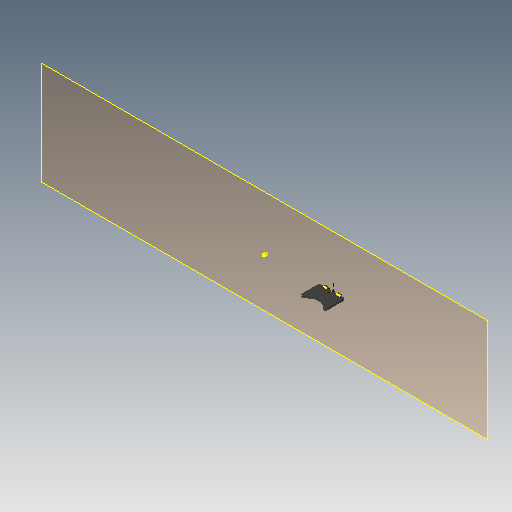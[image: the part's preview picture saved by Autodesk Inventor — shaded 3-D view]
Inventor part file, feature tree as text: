
AUTODESK INVENTOR PART (.ipt)
format: ipt  version: 2017 (Build 210142000, 142)  size: 185,856 bytes
history: native  units: mm
features: sketch x7, extrude x6, fillet x2, reference x2, projected_geometry x2, other x2, plane x1
ambient origin geometry x8: Origin, YZ Plane, XZ Plane, XY Plane, X Axis, Y Axis, Z Axis, Center Point
bodies: Solid1 (feature_tree)
feature tree (22):
  plane  "Work Plane1"
  extrude  "Extrusion1"  Depth=3.0mm
  sketch  "Sketch2"  dims[d2=6.0mm d3=3.0mm]
  extrude  "Extrusion2"  Depth=3.0mm
  extrude  "Extrusion3"  Depth=40.0mm
  fillet  "Fillet1"  Radius=3.0mm
  extrude  "Extrusion4"  Depth=40.0mm
  fillet  "Fillet2"  Radius=38.0mm
  extrude  "Extrusion5"  Depth=16.0mm
  sketch  "Sketch7"  dims[d17=2.0mm d18=40.0mm d19=0.0mm d20=2.0mm d21=1.5mm d22=10.7mm d23=1.5mm d24=6.0mm d25=1.2mm d26=2.0mm d27=40.0mm d28=0.0mm]
  sketch  "Sketch1"  dims[d0=6.0mm d1=3.0mm]
  reference  "Reference1"
  reference  "Reference2"
  projected_geometry  "Projected Loop1"
  projected_geometry  "Projected Loop2"
  sketch  "Sketch3"  dims[d4=3.0mm d5=0.0mm d6=40.0mm d7=3.0mm]
  sketch  "Sketch4"  dims[d8=60.0mm d9=0.0mm d10=40.0mm d11=38.0mm]
  sketch  "Sketch5"  dims[d12=16.0mm d13=16.0mm]
  sketch  "Sketch6"  dims[d14=3.2mm d15=40.0mm d16=0.0mm]
  other  "<userpath>\OneDrive\Inventor\Beast 3D Printer\Extruder Assembly.iam"
  extrude  "Extruder Assembly.iam"  Depth=40.0mm TaperAngle=0.0deg
  other  "Rear Extruder Panel:1"
